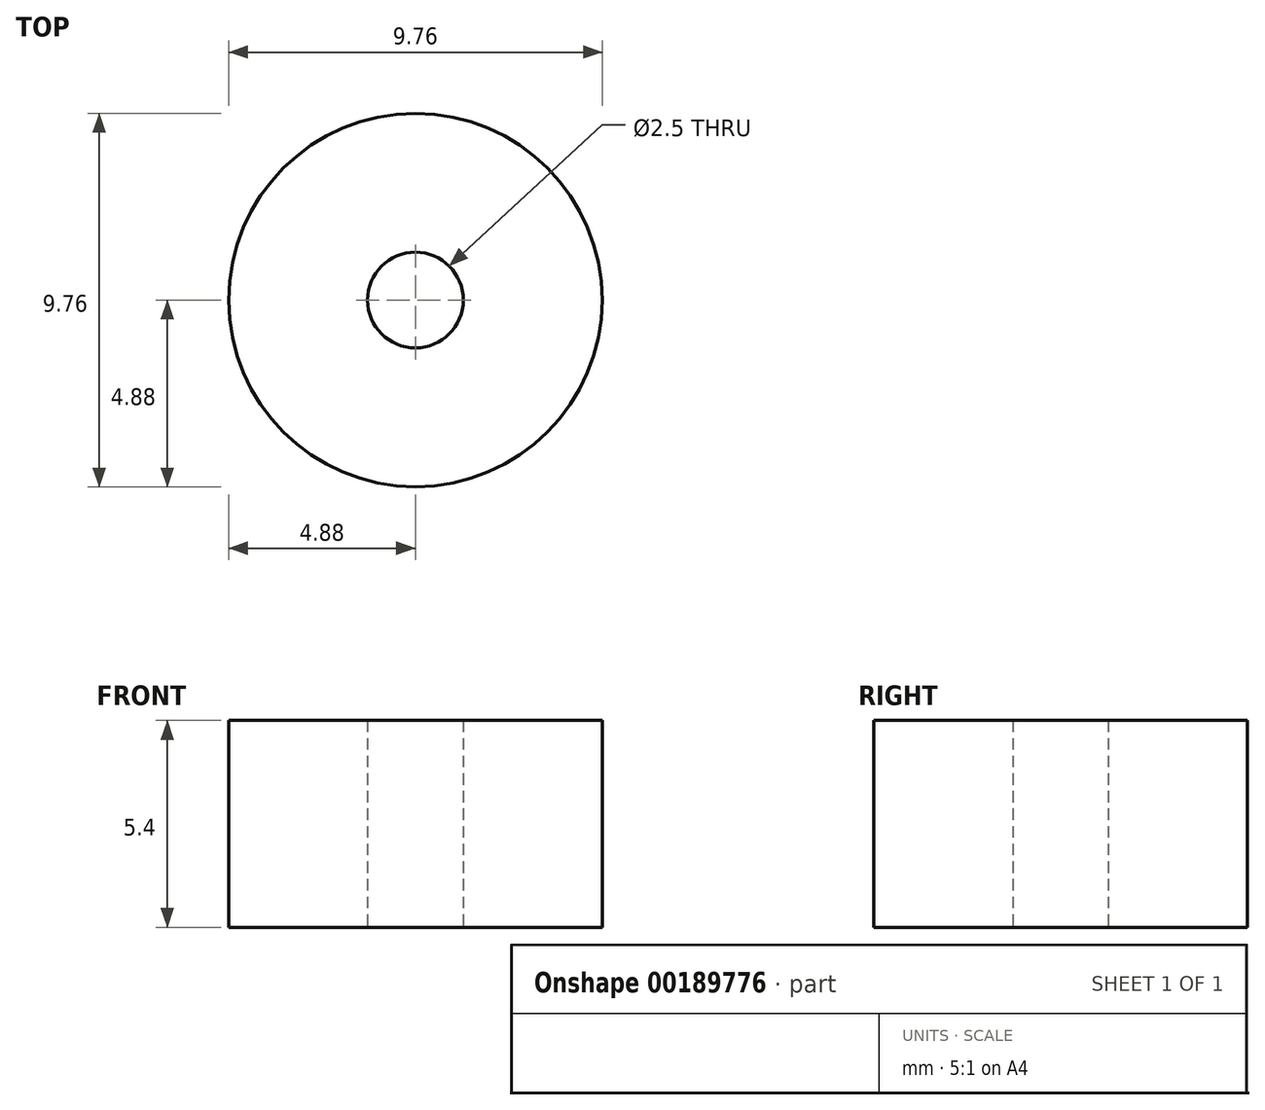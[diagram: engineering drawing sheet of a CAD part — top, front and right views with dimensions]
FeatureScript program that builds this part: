
annotation { "Feature Type Name" : "Feature", "Feature Type Description" : "" }
export const myFeature = defineFeature(function(context is Context, id is Id, definition is map)
    precondition{}
    {
        {
            var Q0;
            Q0=qCreatedBy(makeId("Top.planeOp"),FACE);
            var sketch = newSketch(context, id + "F0", { "sketchPlane" : qUnion([Q0])});
            skCircle(sketch, "E0", {"center": v(0, 0) * mm, "radius": 4.88 * mm});
            skCircle(sketch, "E1", {"center": v(0, 0) * mm, "radius": 1.25 * mm});
            skSolve(sketch);
        }
        {
            var Q0;
            Q0=makeQuery(id+"F0.imprint","IMPRINT",FACE,{"disambiguationData":[TD([[makeQuery(id+"F0.imprint","IMPRINT",EDGE,{"derivedFrom":sQuery(id+"F0.wireOp",EDGE,"E0")}),1.0]])]});
            extrude(context, id + "F1", {"entities" : qUnion([Q0]), "depth" : 5.4 * mm});
        }
    });
